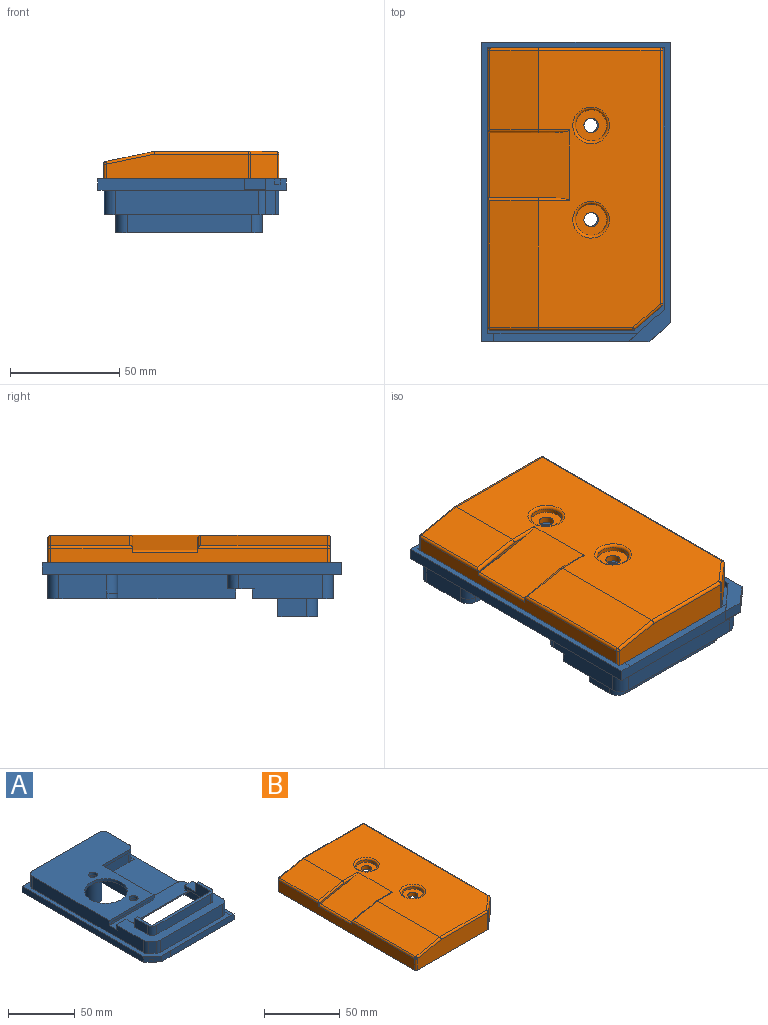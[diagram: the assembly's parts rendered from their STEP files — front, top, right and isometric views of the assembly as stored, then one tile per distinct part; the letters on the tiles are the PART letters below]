
ASSEMBLY  parts=2 mates=1
PART A: 98 faces, bbox 86.7x137.3x30.6 mm
  f0: plane 116.99x11.1mm, normal (-1,0,0), area 1265mm2, adj f1,f3,f7,f10,f27,f68,f82,f83
  f1: plane 80.01x37.19mm, normal (0,0,1), area 999.7mm2, adj f0,f34,f36,f44,f73,f74,f75,f76
  f2: plane 74.93x30.43mm, normal (0,0,-1), area 692.1mm2, adj f5,f32,f42,f45,f76,f77,f78,f84
  f3: plane 2.54x0.03mm, normal (0,1,0), area 0.1mm2, adj f0,f5,f7,f82
  f4: plane 44.7x0.04mm, normal (0,0,-1), area 1.8mm2, adj f15,f33,f61,f68
  f5: plane 115.78x11.37mm, normal (1,0,0), area 1257.1mm2, adj f2,f3,f7,f8,f9,f11,f16,f20
  f6: plane 54.02x11.35mm, normal (-1,0,0), area 613.4mm2, adj f11,f16,f62,f71
  f7: plane 80.01x13.58mm, normal (0,0,1), area 906.8mm2, adj f0,f3,f5,f13,f15,f32,f33,f36
  f8: plane 74.93x10.07mm, normal (0,0,-1), area 754.3mm2, adj f5,f9,f32,f70
  f9: plane 74.93x8.34mm, normal (0,-1,0), area 625mm2, adj f5,f8,f16,f32
  f10: plane 86.11x80.01mm, normal (0,0,1), area 4227.2mm2, adj f0,f12,f15,f18,f39,f57,f58,f59
  f11: plane 80.99x74.93mm, normal (0,0,-1), area 3238.1mm2, adj f5,f6,f17,f43,f52,f55,f59,f62
  f12: plane 27.7x2.55mm, normal (0,-1,0), area 70.3mm2, adj f10,f15,f60,f90
  f13: plane 27.69x6.64mm, normal (0,1,0), area 183.9mm2, adj f7,f15,f19,f92
  f14: plane 3.81x0.01mm, normal (1,0,0), area 0mm2, adj f19,f27,f31
  f15: plane 54.1x11.11mm, normal (1,0,0), area 577.5mm2, adj f4,f7,f10,f12,f13,f19,f60,f61
  f16: plane 74.96x56.59mm, normal (0,0,-1), area 355.2mm2, adj f5,f6,f9,f17,f20,f32,f55,f62
  f17: plane 29.46x11.37mm, normal (-1,0,0), area 306.6mm2, adj f11,f16,f20,f43,f62
  f18: plane 29.46x11.11mm, normal (1,0,0), area 242.8mm2, adj f10,f19,f27,f37,f90,f91,f96
  f19: plane 137.17x35.95mm, normal (0,0,1), area 2090mm2, adj f13,f14,f15,f18,f31,f36,f37,f38
  f20: plane 131.02x81.34mm, normal (0,0,-1), area 2909.2mm2, adj f5,f16,f17,f25,f26,f32,f40,f41
  f21: plane 2.54x0.03mm, normal (1,0,0), area 0.1mm2, adj f23,f29,f46,f47
  f22: plane 2.52x0.07mm, normal (0,1,0), area 0.2mm2, adj f23,f24,f46,f47
  f23: plane 2.6x2.27mm, normal (0,0,-1), area 0.1mm2, adj f21,f22,f46,f47
  f24: plane 4.27x3.67mm, normal (0,0,-1), area 0.4mm2, adj f22,f31,f46,f47
  f25: plane 120.02x2.54mm, normal (1,0,0), area 304.8mm2, adj f20,f29,f41,f48
  f26: plane 68.98x2.54mm, normal (0,1,0), area 174.2mm2, adj f20,f28,f29,f35,f40,f48
  f27: plane 137.16x83.49mm, normal (0,0,1), area 985.7mm2, adj f0,f14,f18,f30,f31,f34,f36,f37
  f28: plane 65.91x3.67mm, normal (0,0,-1), area 234.7mm2, adj f26,f31,f35,f48
  f29: plane 137.26x86.67mm, normal (0,0,-1), area 1043.4mm2, adj f21,f25,f26,f30,f31,f35,f37,f38
  f30: plane 128.64x5.35mm, normal (-1,0,0), area 688.1mm2, adj f27,f29,f37,f46
  f31: plane 77.05x5.35mm, normal (0,-1,0), area 363.7mm2, adj f14,f19,f24,f27,f28,f29,f35,f38
  f32: plane 44.04x11.37mm, normal (-1,0,0), area 430.4mm2, adj f2,f7,f8,f9,f16,f20,f42,f65
  f33: plane 1.93x0.04mm, normal (1,0,0), area 0.1mm2, adj f4,f7,f61,f68
  f34: plane 65.61x11.1mm, normal (0,-1,0), area 728.2mm2, adj f1,f27,f94,f95
  f35: plane 3.67x0.02mm, normal (-1,0,0), area 0.1mm2, adj f26,f28,f29,f31
  f36: plane 43.18x11.11mm, normal (1,0,0), area 396.6mm2, adj f1,f7,f19,f27,f69,f85,f86,f92
  f37: plane 86.67x5.35mm, normal (0,1,0), area 463.6mm2, adj f18,f19,f27,f29,f30,f38
  f38: plane 137.16x5.34mm, normal (1,0,0), area 732mm2, adj f19,f29,f31,f37
  f39: plane 69.85x11.1mm, normal (0,1,0), area 775.3mm2, adj f10,f27,f96,f97
  f40: plane 130.99x2.54mm, normal (-1,0,0), area 332.7mm2, adj f20,f26,f29,f41
  f41: plane 81.31x2.54mm, normal (0,-1,0), area 206.5mm2, adj f20,f25,f29,f40
  f42: plane 65.57x11.37mm, normal (0,1,0), area 745.5mm2, adj f2,f20,f32,f45
  f43: plane 74.93x11.37mm, normal (0,-1,0), area 851.9mm2, adj f5,f11,f17,f20
  f44: plane 11.1x4.24mm, normal (-0.65,-0.76,0), area 62.2mm2, adj f1,f27,f93,f94
  f45: plane 11.37x9.36mm, normal (0.66,0.75,0), area 142mm2, adj f2,f5,f20,f42
  f46: plane 9.61x8.52mm, normal (-0.66,-0.75,0), area 60.1mm2, adj f21,f22,f23,f24,f27,f29,f30,f31
  f47: plane 6.91x6.05mm, normal (-0.66,-0.75,0), area 9.6mm2, adj f21,f22,f23,f24,f29,f31,f49,f50
  f48: plane 16.28x14.74mm, normal (0.67,0.74,0), area 42.3mm2, adj f20,f25,f26,f28,f29,f31,f49,f50
  f49: plane 9.35x5.08mm, normal (0,-1,0), area 47.5mm2, adj f29,f47,f48,f50
  f50: plane 9.46x0.1mm, normal (0,0,1), area 0.9mm2, adj f31,f47,f48,f49
  f51: cylinder r=3.3mm len=19.81mm, axis (0,0,1), area 411mm2, adj f53,f58
  f52: cylinder r=6.48mm len=19.81mm, axis (0,0,1), area 806.3mm2, adj f11,f53
  f53: plane 12.95x12.95mm, normal (0,0,-1), area 97.5mm2, adj f51,f52
  f54: cylinder r=3.3mm len=19.81mm, axis (0,0,1), area 411mm2, adj f56,f57
  f55: cylinder r=6.48mm len=19.81mm, axis (0,0,1), area 706.4mm2, adj f11,f16,f56,f71,f72
  f56: plane 12.95x12.95mm, normal (0,0,-1), area 97.5mm2, adj f54,f55
  f57: cylinder r=3.29mm len=6.59mm, axis (0,0,-1), area 52.6mm2, adj f10,f54
  f58: cylinder r=3.3mm len=6.6mm, axis (0,0,-1), area 52.7mm2, adj f10,f51
  f59: cylinder r=16mm len=32mm, axis (0,0,1), area 255.4mm2, adj f10,f11
  f60: plane 27.7x8.58mm, normal (0,-1,0), area 237.3mm2, adj f12,f15,f19,f91
  f61: plane 44.7x1.93mm, normal (0,-1,0), area 86.3mm2, adj f4,f7,f15,f33
  f62: plane 32.77x11.35mm, normal (0,1,0), area 372mm2, adj f6,f11,f16,f17
  f63: plane 50.55x0.02mm, normal (-1,0,0), area 0.8mm2, adj f16,f20,f64,f65
  f64: plane 1.38x0.02mm, normal (0,1,0), area 0mm2, adj f16,f20,f63
  f65: plane 31.6x0.02mm, normal (0,-1,0), area 0.5mm2, adj f16,f20,f32,f63
  f66: plane 5.6x2.52mm, normal (0,0,1), area 6.4mm2, adj f19,f91
  f67: plane 5.63x2.56mm, normal (0,0,1), area 6.3mm2, adj f19,f92
  f68: plane 47.24x4.47mm, normal (0,-1,0), area 124.9mm2, adj f0,f4,f7,f10,f15,f33
  f69: plane 2.54x0.03mm, normal (0,1,0), area 0.1mm2, adj f7,f32,f36,f85
  f70: plane 74.93x1.08mm, normal (0,-1,0), area 81.1mm2, adj f5,f7,f8,f32
  f71: plane 11.35x7.26mm, normal (0,1,0), area 82.4mm2, adj f6,f11,f16,f55
  f72: plane 26.76x11.35mm, normal (0,1,0), area 303.9mm2, adj f5,f11,f16,f55
  f73: plane 56.95x8.26mm, normal (0,-1,0), area 470.1mm2, adj f1,f81,f88,f89
  f74: plane 13.1x8.26mm, normal (1,0,0), area 108.2mm2, adj f1,f75,f81,f88
  f75: plane 8.26x2.54mm, normal (0,1,0), area 21mm2, adj f1,f74,f76,f81
  f76: plane 27.51x12.7mm, normal (-1,0,0), area 203.8mm2, adj f1,f2,f75,f77,f81,f85,f86,f87
  f77: plane 62.04x10.8mm, normal (0,1,0), area 669.7mm2, adj f2,f76,f78,f81
  f78: plane 27.51x12.7mm, normal (1,0,0), area 203.8mm2, adj f1,f2,f77,f79,f81,f82,f83,f84
  f79: plane 8.26x2.53mm, normal (0,1,0), area 20.9mm2, adj f1,f78,f80,f81
  f80: plane 13.1x8.26mm, normal (-1,0,0), area 108.2mm2, adj f1,f79,f81,f89
  f81: plane 67.11x18.18mm, normal (0,0,1), area 238.8mm2, adj f73,f74,f75,f76,f77,f78,f79,f80
  f82: plane 10.16x2.54mm, normal (0,0,-1), area 21.7mm2, adj f0,f3,f5,f78,f83,f84
  f83: plane 10.16x4.45mm, normal (0,1,0), area 45.1mm2, adj f0,f1,f78,f82
  f84: plane 7.62x1.91mm, normal (0,-1,0), area 14.5mm2, adj f2,f5,f78,f82
  f85: plane 7.81x2.54mm, normal (0,0,-1), area 15.8mm2, adj f32,f36,f69,f76,f86,f87
  f86: plane 7.81x4.45mm, normal (0,1,0), area 34.7mm2, adj f1,f36,f76,f85
  f87: plane 5.27x1.91mm, normal (0,-1,0), area 10mm2, adj f2,f32,f76,f85
  f88: cylinder r=5.08mm len=8.26mm, axis (0,0,-1), area 65.9mm2, adj f1,f73,f74,f81
  f89: cylinder r=5.08mm len=8.26mm, axis (0,0,-1), area 65.9mm2, adj f1,f73,f80,f81
  f90: cylinder r=5.08mm len=5.08mm, axis (0,0,-1), area 20.3mm2, adj f10,f12,f18,f91
  f91: cylinder r=5.08mm len=8.57mm, axis (0,0,1), area 68.4mm2, adj f18,f19,f60,f66,f90
  f92: cylinder r=5.08mm len=6.64mm, axis (0,0,1), area 53mm2, adj f7,f13,f19,f36,f67
  f93: cylinder r=5.08mm len=11.1mm, axis (0,0,1), area 48.4mm2, adj f0,f1,f27,f44
  f94: cylinder r=5.08mm len=11.1mm, axis (0,0,-1), area 40.1mm2, adj f1,f27,f34,f44
  f95: cylinder r=5.08mm len=11.1mm, axis (0,0,1), area 88.6mm2, adj f1,f27,f34,f36
  f96: cylinder r=5.08mm len=11.1mm, axis (0,0,1), area 88.6mm2, adj f10,f18,f27,f39
  f97: cylinder r=5.08mm len=11.1mm, axis (0,0,-1), area 88.6mm2, adj f0,f10,f27,f39
PART B: 76 faces, bbox 80.7x129.5x15.2 mm
  f0: plane 83.82x54.61mm, normal (0,0,-1), area 3580.8mm2, adj f11,f12,f13,f14,f15,f21,f22,f23
  f1: plane 54.61x10.16mm, normal (0,0,-1), area 554.8mm2, adj f11,f12,f25,f66
  f2: plane 65.35x13.84mm, normal (0,-1,0), area 853.7mm2, adj f4,f42,f48,f50,f51
  f3: plane 116.19x13.84mm, normal (1,0,0), area 1608.4mm2, adj f4,f53,f57,f59
  f4: plane 129.54x80.39mm, normal (0,0,-1), area 979.2mm2, adj f2,f3,f5,f6,f9,f10,f11,f19
  f5: plane 3.38x0.05mm, normal (0,-1,0), area 0.2mm2, adj f4,f7,f36,f37
  f6: plane 2.94x0.05mm, normal (1,0,0), area 0.2mm2, adj f4,f7,f36,f37
  f7: plane 8.26x7.16mm, normal (0,0,-1), area 19.3mm2, adj f5,f6,f36,f37
  f8: plane 54.61x20.32mm, normal (0,0,-1), area 1055.4mm2, adj f9,f11,f13,f36,f68
  f9: plane 64.27x12.52mm, normal (0,1,0), area 759.2mm2, adj f4,f8,f10,f13,f36
  f10: plane 124.46x8.17mm, normal (1,0,0), area 895.3mm2, adj f4,f9,f12,f13,f21,f22,f23,f25
  f11: plane 114.76x12.52mm, normal (-1,0,0), area 1391.7mm2, adj f0,f1,f4,f8,f25,f36,f65,f66
  f12: plane 36.32x20.85mm, normal (0.2,0,-0.98), area 756.4mm2, adj f0,f1,f10,f15,f21,f25,f64,f65
  f13: plane 58.17x20.85mm, normal (0.2,0,-0.98), area 1145.2mm2, adj f0,f8,f9,f10,f14,f22,f67,f68
  f14: plane 30.62x6.73mm, normal (0,1,0), area 30.1mm2, adj f0,f13,f19,f24,f38,f40,f62
  f15: plane 30.62x6.73mm, normal (0,-1,0), area 30.1mm2, adj f0,f12,f19,f24,f39,f41,f62
  f16: plane 127x55.88mm, normal (0,0,1), area 6120.9mm2, adj f17,f18,f24,f38,f39,f51,f52,f56
  f17: plane 36.32x22.23mm, normal (-0.2,0,0.98), area 824.8mm2, adj f16,f41,f44,f49
  f18: plane 58.17x22.23mm, normal (-0.2,0,0.98), area 1320.9mm2, adj f16,f40,f43,f48
  f19: plane 127x9.23mm, normal (-1,0,0), area 1109.2mm2, adj f4,f14,f15,f40,f41,f42,f43,f44
  f20: plane 77.85x13.84mm, normal (0,1,0), area 1026.8mm2, adj f4,f45,f49,f52,f53
  f21: plane 35.09x7.08mm, normal (0,1,0), area 78.8mm2, adj f0,f10,f12,f23,f24
  f22: plane 35.09x7.08mm, normal (0,-1,0), area 78.8mm2, adj f0,f10,f13,f23,f24
  f23: plane 35.09x29.97mm, normal (0.2,0,-0.98), area 1072.8mm2, adj f0,f10,f21,f22
  f24: plane 36.44x32.51mm, normal (-0.18,0,0.98), area 1114.4mm2, adj f14,f15,f16,f21,f22,f38,f39,f62
  f25: plane 75.46x12.52mm, normal (0,-1,0), area 899.3mm2, adj f1,f4,f10,f11,f12
  f26: cylinder r=9.53mm len=19.05mm, axis (0,0,1), area 127.5mm2, adj f0,f75
  f27: plane 16.51x16.51mm, normal (0,0,-1), area 179.8mm2, adj f33,f75
  f28: cylinder r=9.53mm len=19.05mm, axis (0,0,1), area 127.5mm2, adj f0,f74
  f29: plane 16.51x16.51mm, normal (0,0,-1), area 179.8mm2, adj f30,f74
  f30: cylinder r=3.3mm len=6.6mm, axis (0,0,1), area 61.1mm2, adj f29,f31
  f31: plane 14.3x14.3mm, normal (0,0,1), area 126.4mm2, adj f30,f32
  f32: cylinder r=7.15mm len=14.3mm, axis (0,0,1), area 79.9mm2, adj f31,f60
  f33: cylinder r=3.3mm len=6.6mm, axis (0,0,1), area 61.1mm2, adj f27,f34
  f34: plane 14.3x14.3mm, normal (0,0,1), area 126.4mm2, adj f33,f35
  f35: cylinder r=7.15mm len=14.3mm, axis (0,0,1), area 79.9mm2, adj f34,f61
  f36: plane 12.57x11.19mm, normal (-0.65,0.76,0), area 186mm2, adj f4,f5,f6,f7,f8,f9,f11
  f37: plane 13.9x12.5mm, normal (0.65,-0.76,0), area 229.2mm2, adj f4,f5,f6,f7,f50,f56,f59
  f38: cylinder r=1.27mm len=14.23mm, axis (-1,0,0), area 23.3mm2, adj f14,f16,f24,f40
  f39: cylinder r=1.27mm len=14.23mm, axis (1,0,0), area 23.3mm2, adj f15,f16,f24,f41
  f40: cylinder r=1.27mm len=23.76mm, axis (-0.98,0,-0.2), area 46.8mm2, adj f14,f18,f19,f38,f43
  f41: cylinder r=1.27mm len=23.76mm, axis (0.98,0,0.2), area 46.8mm2, adj f15,f17,f19,f39,f44
  f42: cylinder r=1.27mm len=9.23mm, axis (0,0,1), area 18.4mm2, adj f2,f4,f19,f46
  f43: cylinder r=1.27mm len=59.41mm, axis (0,1,0), area 102.1mm2, adj f18,f19,f40,f46
  f44: cylinder r=1.27mm len=37.57mm, axis (0,1,0), area 64.3mm2, adj f17,f19,f41,f47
  f45: cylinder r=1.27mm len=9.23mm, axis (0,0,-1), area 18.4mm2, adj f4,f19,f20,f47
  f46: sphere r=1.27mm, area 2.2mm2, adj f42,f43,f48
  f47: sphere r=1.27mm, area 2.2mm2, adj f44,f45,f49
  f48: cylinder r=1.27mm len=22.49mm, axis (0.98,0,0.2), area 45.2mm2, adj f2,f18,f46,f51
  f49: cylinder r=1.27mm len=22.49mm, axis (-0.98,0,-0.2), area 45.2mm2, adj f17,f20,f47,f52
  f50: cylinder r=1.27mm len=13.84mm, axis (0,0,1), area 12.5mm2, adj f2,f4,f37,f54
  f51: cylinder r=1.27mm len=43.38mm, axis (1,0,0), area 86.4mm2, adj f2,f16,f48,f54
  f52: cylinder r=1.27mm len=55.88mm, axis (-1,0,0), area 111.4mm2, adj f16,f20,f49,f55
  f53: cylinder r=1.27mm len=13.84mm, axis (0,0,1), area 27.6mm2, adj f3,f4,f20,f55
  f54: sphere r=1.27mm, area 1.2mm2, adj f50,f51,f56
  f55: sphere r=1.27mm, area 2.5mm2, adj f52,f53,f57
  f56: cylinder r=1.27mm len=13.33mm, axis (-0.76,-0.65,0), area 33mm2, adj f16,f37,f54,f58
  f57: cylinder r=1.27mm len=116.19mm, axis (0,1,0), area 231.8mm2, adj f3,f16,f55,f58
  f58: sphere r=1.27mm, area 1.4mm2, adj f56,f57,f59
  f59: cylinder r=1.27mm len=13.84mm, axis (0,0,-1), area 15.1mm2, adj f3,f4,f37,f58
  f60: torus R=8.42mm, axis (0,0,-1), area 95.4mm2, adj f16,f32
  f61: torus R=8.42mm, axis (0,0,-1), area 95.4mm2, adj f16,f35
  f62: cylinder r=1.27mm len=29.97mm, axis (0,-1,0), area 52.8mm2, adj f14,f15,f19,f24
  f63: plane 5.08x1.58mm, normal (-0.98,0,0.21), area 8.2mm2, adj f10,f64,f65,f66
  f64: plane 17.18x5.08mm, normal (-0.21,0,0.98), area 89.3mm2, adj f12,f63,f65,f66
  f65: plane 75.46x7.03mm, normal (0,-1,0), area 190mm2, adj f0,f10,f11,f12,f63,f64,f72,f73
  f66: plane 75.46x7.03mm, normal (0,1,0), area 190mm2, adj f1,f10,f11,f12,f63,f64,f72,f73
  f67: plane 5.08x2.77mm, normal (-0.22,0,0.98), area 14.4mm2, adj f10,f13,f68,f69
  f68: plane 75.46x7.13mm, normal (0,-1,0), area 179mm2, adj f8,f10,f11,f13,f67,f70,f71
  f69: plane 75.46x7.13mm, normal (0,1,0), area 179mm2, adj f0,f10,f11,f13,f67,f70,f71
  f70: cylinder r=2.54mm len=21.7mm, axis (-0.97,0,-0.23), area 169.9mm2, adj f10,f68,f69,f71
  f71: cylinder r=2.54mm len=54.92mm, axis (-1,0,0), area 436.8mm2, adj f11,f68,f69,f70
  f72: cylinder r=2.54mm len=21.59mm, axis (-0.98,0,-0.21), area 168.9mm2, adj f10,f65,f66,f73
  f73: cylinder r=2.54mm len=54.96mm, axis (-1,0,0), area 437.2mm2, adj f11,f65,f66,f72
  f74: torus R=8.26mm, axis (0,0,1), area 113.6mm2, adj f28,f29
  f75: torus R=8.26mm, axis (0,0,1), area 113.6mm2, adj f26,f27
PLACE A rot(axis=(0,-1,0),180deg) t=(16.73,-119.3,100.82)mm
PLACE B t=(79.05,-121.84,89.26)mm
MATE parallel A.f20 <-> B.f4  axis (0,0,1) through (86.38,-124.38,97.17)mm
